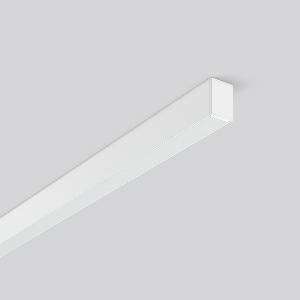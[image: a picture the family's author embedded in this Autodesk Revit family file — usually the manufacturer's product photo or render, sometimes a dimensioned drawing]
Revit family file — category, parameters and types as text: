
# Revit family: less_is_more_27_312197_002_76_f4b8
name_source: partatom
category: Lighting Fixtures
units: mm (PartAtom-declared; Revit-internal decimal feet)

## family parameters
Cut with Voids When Loaded = No
Host = Face
Light Source = No
Part Type = Normal
Room Calculation Point = No
Round Connector Dimension = Use Diameter
Shared = No

## types (1)
- LESS IS MORE 27 (1 x LED Modul 830, 2150 lm, 3000)
    Apparent Load = 29 VA
    CIE Flux Codes = 65 89 98 100 100
    Color Rendering = 80
    Color Temperature = 3000
    Default Elevation = 1800 mm
    Description = Series: LESS IS MORE 27
Ceiling luminaire with slim design. Housing: extruded aluminium profile, powder-coated. End cap aluminium powder-coated. Diffuser made of non-yellowing plastic (PMMA) microprismatic. Suitable for Ceiling mounting, Wall (surface). External driver with connecting cable. 
Colour: traffic white, matt (RAL 9016)
Length: 1012 mm
Width: 28 mm
Height: 38 mm
Lamp: LED
Socket: without socket
Colour temperature: 3000K
Colour rendering index (CRI): 82
System power: 29 W
Rated luminous flux: 2150 lm
Luminous efficiency: 74 lm/W
Control gear: Voltage converter, DALI dim.
Protection class: II
Type of protection: IP 20
    Height = 38 mm
    Lamp = 1 x LED Modul 830
    Lamp Light Flux = 2150 lm
    Lamp count = 1
    Length = 1012 mm
    Lifetime = 50000 h
    Luminous efficacy = 74 lm/W
    Manufacturer = RZB
    ModVariant = No
    Model = 312197.002.76
    Mounting Place = Ceiling, Wall
    Mounting Type = Surface mounted
    Number of Poles = 1
    OnlyDefault = Yes
    Power Factor = 1
    Product Name = LESS IS MORE 27
    Product group = Surface mounted LED linear luminaires
    ProductGroupID = 307
    Protection Class = Protection class II
    Protection Degree = IP 20
    RLX_Detail_Level = 1
    RLX_Emergency_Light_Flux = 0 lm
    RLX_Emergency_Type = 0
    RLX_Emergency_Type_DB = No
    RlxData = <blob elided: 23933 chars, md5=05c705f2>
    Socket = socket
    Standby Power = 0 W
    System Light Flux = 2150 lm
    System Power = 29 W
    Type Comments = Product without accessories
    Type Image = 312196.002.jpg
    URL = http://relux.com
    VarID = ---
    Voltage = 230 V
    Voltage Range = 220-240 V
    Weight = 0.00 kg
    Width = 28 mm

## geometry (parser evidence)
native form markers: Blend x4, Sweep x12
no freeform markers — native parametric forms only
